# Revit family: LCS6337A75T,A2T,A75B,A2B
name_source: partatom
category: Plumbing Fixtures
revit_build: Autodesk Revit LT 2014 (Build: 20130308_1515(x64)
units: mm (PartAtom-declared; Revit-internal decimal feet)

## types (4) — shared parameters
Assembly Code = D2010710
Keynote = 22 40 00.B3
Manufacturer = Best Bath Systems, Inc.
Type Comments = ADA Compliant
URL = http://www.best-bath.com
Unit Width = 5' - 3"

## per-type parameters (varying)
| type | Description | Model | Threshold Height | Unit Height |
| LCS6337A75B | Classic Tile, Beveled Threshold | LCS6337A75B | 0' - 0 3/4" | 6' - 6 1/2" |
| LCS6337A2B | Classic Tile, Beveled Threshold | LCS6337A75B | 0' - 2" | 6' - 8" |
| LCS6337A75T | Classic Tile, Traditional Bull Nose Threshold | LCS6337A75T | 0' - 0 3/4" | 6' - 6 1/2" |
| LCS6337A2T | Classic Tile, Traditional Bull Nose Threshold | LCS6337A75T | 0' - 2" | 6' - 8" |

## geometry (parser evidence)
native form markers: Blend x27, Sweep x5
no freeform markers — native parametric forms only
